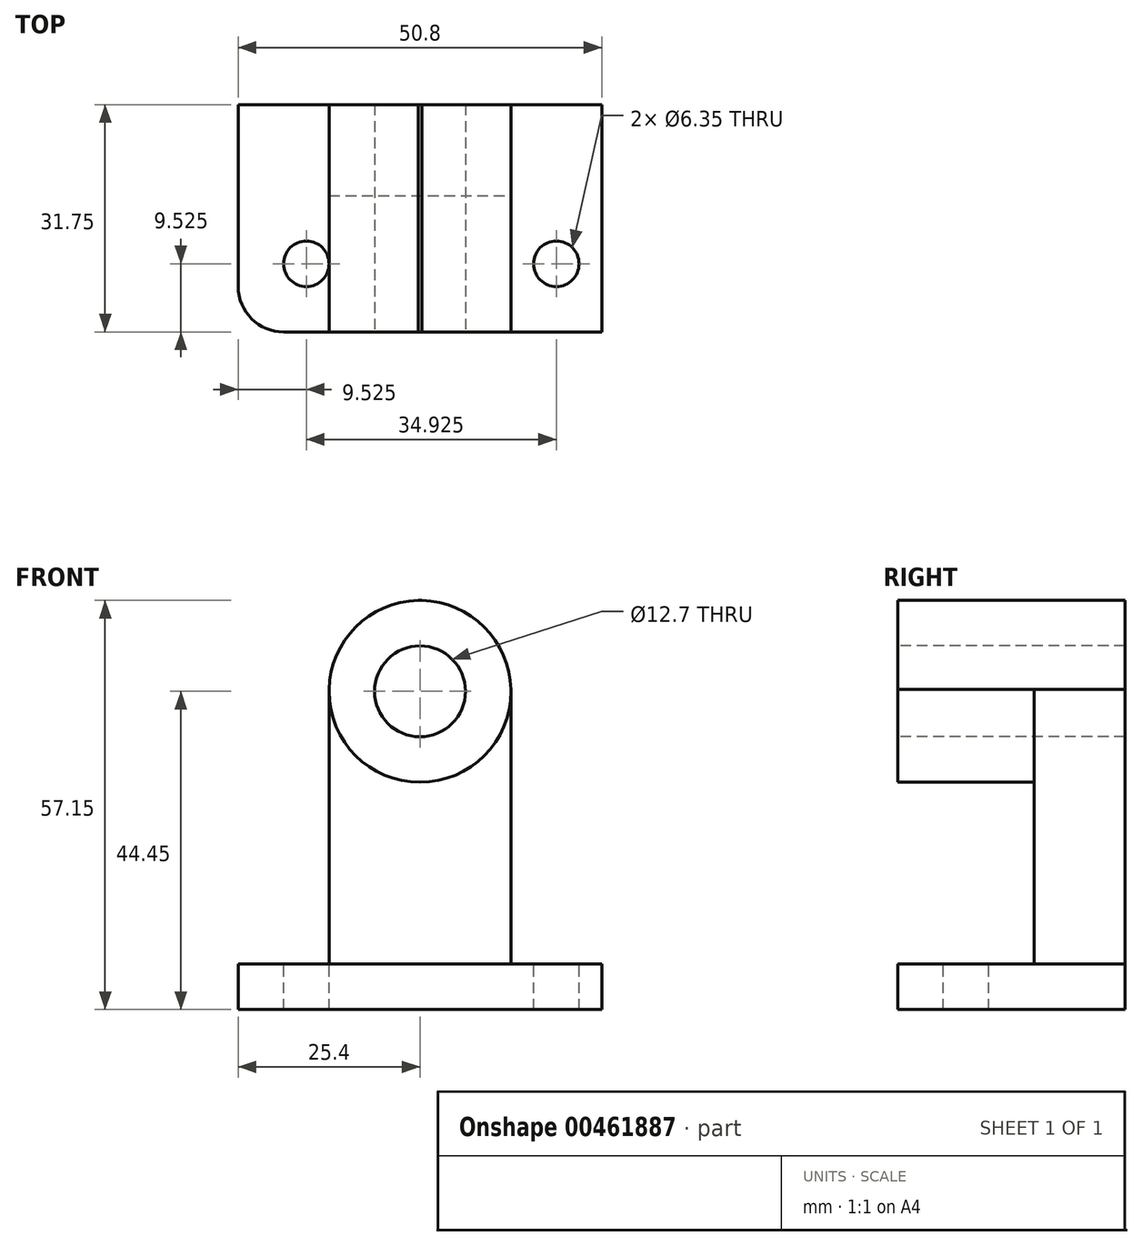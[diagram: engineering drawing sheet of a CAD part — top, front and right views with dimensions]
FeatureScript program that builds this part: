
annotation { "Feature Type Name" : "Feature", "Feature Type Description" : "" }
export const myFeature = defineFeature(function(context is Context, id is Id, definition is map)
    precondition{}
    {
        {
            var Q0;
            Q0=qCreatedBy(makeId("Front.planeOp"),FACE);
            var sketch = newSketch(context, id + "F0", { "sketchPlane" : qUnion([Q0])});
            skLineSegment(sketch, "E0.bottom", {"start": v(0, 0) * mm, "end": v(50.8, 0) * mm});
            skLineSegment(sketch, "E0.top", {"start": v(0, 57.15) * mm, "end": v(50.8, 57.15) * mm});
            skLineSegment(sketch, "E0.left", {"start": v(0, 0) * mm, "end": v(0, 57.15) * mm});
            skLineSegment(sketch, "E0.right", {"start": v(50.8, 0) * mm, "end": v(50.8, 57.15) * mm});
            skSolve(sketch);
        }
        {
            var Q0;
            Q0 = qSketchRegion(id + "F0", true);
            extrude(context, id + "F1", {"entities" : qUnion([Q0]), "depth" : 31.75 * mm});
        }
        {
            var Q0;
            Q0=makeQuery(id+"F1.opExtrude","CAP_FACE",FACE,{"disambiguationData":[OSD([sQuery(id+"F0.wireOp",EDGE,"E0.bottom"),sQuery(id+"F0.wireOp",EDGE,"E0.top"),sQuery(id+"F0.wireOp",EDGE,"E0.left"),sQuery(id+"F0.wireOp",EDGE,"E0.right")])],"isStart":false});
            var sketch = newSketch(context, id + "F2", { "sketchPlane" : qUnion([Q0])});
            skLineSegment(sketch, "E1", {"start": v(12.7, 57.15) * mm, "end": v(12.7, 6.35) * mm});
            skLineSegment(sketch, "E2", {"start": v(12.7, 6.35) * mm, "end": v(0, 6.35) * mm});
            skLineSegment(sketch, "E3", {"start": v(38.1, 57.15) * mm, "end": v(38.1, 6.35) * mm});
            skLineSegment(sketch, "E4", {"start": v(38.1, 6.35) * mm, "end": v(50.8, 6.35) * mm});
            skSolve(sketch);
        }
        {
            var Q0;
            {var subQ0=sQuery(id+"F2.wireOp",EDGE,"E1");Q0=makeQuery(id+"F2.imprint","IMPRINT",FACE,{"disambiguationData":[TD([[makeQuery(id+"F2.imprint","IMPRINT",EDGE,{"derivedFrom":subQ0}),-1.0]])]});}
            var Q1;
            {var subQ0=sQuery(id+"F2.wireOp",EDGE,"E3");Q1=makeQuery(id+"F2.imprint","IMPRINT",FACE,{"disambiguationData":[TD([[makeQuery(id+"F2.imprint","IMPRINT",EDGE,{"derivedFrom":subQ0}),1.0]])]});}
            extrude(context, id + "F3", {"entities" : qUnion([Q0, Q1]), "operationType" : NewBodyOperationType.REMOVE, "oppositeDirection" : true, "depth" : 31.75 * mm});
        }
        {
            var Q0;
            Q0=makeQuery(id+"F1.opExtrude","CAP_FACE",FACE,{"disambiguationData":[OSD([sQuery(id+"F0.wireOp",EDGE,"E0.bottom"),sQuery(id+"F0.wireOp",EDGE,"E0.top"),sQuery(id+"F0.wireOp",EDGE,"E0.left"),sQuery(id+"F0.wireOp",EDGE,"E0.right")])],"isStart":false});
            var sketch = newSketch(context, id + "F4", { "sketchPlane" : qUnion([Q0])});
            skLineSegment(sketch, "E5", {"start": v(12.7, 6.35) * mm, "end": v(38.1, 6.35) * mm});
            skCircle(sketch, "E6", {"center": v(25.4, 44.45) * mm, "radius": 12.7 * mm});
            skSolve(sketch);
        }
        {
            var Q0;
            {var subQ0=sQuery(id+"F4.wireOp",EDGE,"E5");Q0=makeQuery(id+"F4.imprint","IMPRINT",FACE,{"disambiguationData":[TD([[makeQuery(id+"F4.imprint","IMPRINT",EDGE,{"derivedFrom":subQ0}),1.0]])]});}
            extrude(context, id + "F5", {"entities" : qUnion([Q0]), "operationType" : NewBodyOperationType.REMOVE, "oppositeDirection" : true, "depth" : 19.05 * mm});
        }
        {
            var Q0;
            {var subQ0=sQuery(id+"F0.wireOp",EDGE,"E0.top");Q0=makeQuery(id+"F5.boolean.opBoolean","SPLIT",FACE,{"disambiguationData":[TD([makeQuery(id+"F1.opExtrude","SWEPT_FACE",FACE,{"disambiguationData":[OSD([subQ0])]})])],"derivedFrom":makeQuery(id+"F1.opExtrude","CAP_FACE",FACE,{"disambiguationData":[OSD([sQuery(id+"F0.wireOp",EDGE,"E0.bottom"),subQ0,sQuery(id+"F0.wireOp",EDGE,"E0.left"),sQuery(id+"F0.wireOp",EDGE,"E0.right")])],"isStart":false})});}
            var sketch = newSketch(context, id + "F6", { "sketchPlane" : qUnion([Q0])});
            skCircle(sketch, "E7", {"center": v(25.4, 44.45) * mm, "radius": 12.7 * mm});
            skSolve(sketch);
        }
        {
            var Q0;
            {var subQ0=sQuery(id+"F6.wireOp",EDGE,"E7");var subQ1=makeQuery(id+"F1.opExtrude","CAP_EDGE",EDGE,{"disambiguationData":[OSD([sQuery(id+"F0.wireOp",EDGE,"E0.top")])],"isStart":false});var subQ2=makeQuery(id+"F6.imprint","INTERSECT",VERTEX,{"disambiguationData":[OD(1.0)],"derivedFrom":[subQ1,subQ0]});Q0=makeQuery(id+"F6.imprint","IMPRINT",FACE,{"disambiguationData":[TD([[makeQuery(id+"F6.imprint","IMPRINT",EDGE,{"disambiguationData":[TD([[subQ2,-1.0]])],"derivedFrom":subQ0}),-1.0]])]});}
            var Q1;
            {var subQ0=sQuery(id+"F6.wireOp",EDGE,"E7");var subQ1=makeQuery(id+"F1.opExtrude","CAP_EDGE",EDGE,{"disambiguationData":[OSD([sQuery(id+"F0.wireOp",EDGE,"E0.top")])],"isStart":false});var subQ2=makeQuery(id+"F6.imprint","INTERSECT",VERTEX,{"disambiguationData":[OD(0.0)],"derivedFrom":[subQ1,subQ0]});Q1=makeQuery(id+"F6.imprint","IMPRINT",FACE,{"disambiguationData":[TD([[makeQuery(id+"F6.imprint","IMPRINT",EDGE,{"disambiguationData":[TD([[subQ2,1.0]])],"derivedFrom":subQ0}),-1.0]])]});}
            extrude(context, id + "F7", {"entities" : qUnion([Q0, Q1]), "operationType" : NewBodyOperationType.REMOVE, "oppositeDirection" : true, "depth" : 31.75 * mm});
        }
        {
            var Q0;
            Q0=makeQuery(id+"F5.boolean.opBoolean","MERGE",FACE,{"derivedFrom":[makeQuery(id+"F3.boolean.opBoolean","COPY",FACE,{"derivedFrom":makeQuery(id+"F3.opExtrude","SWEPT_FACE",FACE,{"disambiguationData":[OSD([sQuery(id+"F2.wireOp",EDGE,"E2")])]})}),makeQuery(id+"F3.boolean.opBoolean","COPY",FACE,{"derivedFrom":makeQuery(id+"F3.opExtrude","SWEPT_FACE",FACE,{"disambiguationData":[OSD([sQuery(id+"F2.wireOp",EDGE,"E4")])]})}),makeQuery(id+"F5.opExtrude","SWEPT_FACE",FACE,{"disambiguationData":[OSD([sQuery(id+"F4.wireOp",EDGE,"E5")])]})]});
            var sketch = newSketch(context, id + "F8", { "sketchPlane" : qUnion([Q0])});
            skCircle(sketch, "E8", {"center": v(44.45, -22.23) * mm, "radius": 3.18 * mm});
            skCircle(sketch, "E9", {"center": v(9.53, -22.23) * mm, "radius": 3.18 * mm});
            skLineSegment(sketch, "E10", {"start": v(0, 0) * mm, "end": v(0, -25.4) * mm});
            skLineSegment(sketch, "E11", {"start": v(6.35, -31.75) * mm, "end": v(50.8, -31.75) * mm});
            skLineSegment(sketch, "E12", {"start": v(50.8, -25.4) * mm, "end": v(50.8, 0) * mm});
            skPoint(sketch, "E13.visualSharp", {"position": v(0, -31.75) * mm});
            skArc(sketch, "E13.filletArc", {"start": v(0, -25.4) * mm, "mid": v(1.86, -29.9) * mm, "end": v(6.35, -31.75) * mm});
            skLineSegment(sketch, "E14", {"start": v(44.45, -31.75) * mm, "end": v(0, -31.75) * mm});
            skPoint(sketch, "E15.visualSharp", {"position": v(50.8, -31.75) * mm});
            skArc(sketch, "E15.filletArc", {"start": v(44.45, -31.75) * mm, "mid": v(48.94, -29.9) * mm, "end": v(50.8, -25.4) * mm});
            skSolve(sketch);
        }
        {
            var Q0;
            Q0=makeQuery(id+"F8.imprint","IMPRINT",FACE,{"disambiguationData":[TD([[makeQuery(id+"F8.imprint","IMPRINT",EDGE,{"derivedFrom":sQuery(id+"F8.wireOp",EDGE,"E9")}),1.0]])]});
            var Q1;
            {var subQ0=sQuery(id+"F8.wireOp",EDGE,"E13.filletArc");Q1=makeQuery(id+"F8.imprint","IMPRINT",FACE,{"disambiguationData":[TD([[makeQuery(id+"F8.imprint","IMPRINT",EDGE,{"derivedFrom":subQ0}),-1.0]])]});}
            var Q2;
            Q2=makeQuery(id+"F8.imprint","IMPRINT",FACE,{"disambiguationData":[TD([[makeQuery(id+"F8.imprint","IMPRINT",EDGE,{"derivedFrom":sQuery(id+"F8.wireOp",EDGE,"E8")}),1.0]])]});
            var Q3;
            {var subQ0=sQuery(id+"F8.wireOp",EDGE,"E11");Q3=makeQuery(id+"F8.imprint","IMPRINT",FACE,{"disambiguationData":[TD([[makeQuery(id+"F8.imprint","IMPRINT",EDGE,{"derivedFrom":subQ0}),1.0]])]});}
            extrude(context, id + "F9", {"entities" : qUnion([Q0, Q1, Q2, Q3]), "operationType" : NewBodyOperationType.REMOVE, "oppositeDirection" : true, "depth" : 6.35 * mm});
        }
        {
            var Q0;
            {var subQ0=sQuery(id+"F0.wireOp",EDGE,"E0.top");Q0=makeQuery(id+"F5.boolean.opBoolean","SPLIT",FACE,{"disambiguationData":[TD([makeQuery(id+"F1.opExtrude","SWEPT_FACE",FACE,{"disambiguationData":[OSD([subQ0])]})])],"derivedFrom":makeQuery(id+"F1.opExtrude","CAP_FACE",FACE,{"disambiguationData":[OSD([sQuery(id+"F0.wireOp",EDGE,"E0.bottom"),subQ0,sQuery(id+"F0.wireOp",EDGE,"E0.left"),sQuery(id+"F0.wireOp",EDGE,"E0.right")])],"isStart":false})});}
            var sketch = newSketch(context, id + "F10", { "sketchPlane" : qUnion([Q0])});
            skCircle(sketch, "E16", {"center": v(25.4, 44.45) * mm, "radius": 6.35 * mm});
            skSolve(sketch);
        }
        {
            var Q0;
            Q0=makeQuery(id+"F10.imprint","IMPRINT",FACE,{"disambiguationData":[TD([[makeQuery(id+"F10.imprint","IMPRINT",EDGE,{"derivedFrom":sQuery(id+"F10.wireOp",EDGE,"E16")}),1.0]])]});
            extrude(context, id + "F11", {"entities" : qUnion([Q0]), "operationType" : NewBodyOperationType.REMOVE, "oppositeDirection" : true, "depth" : 31.75 * mm});
        }
    });
